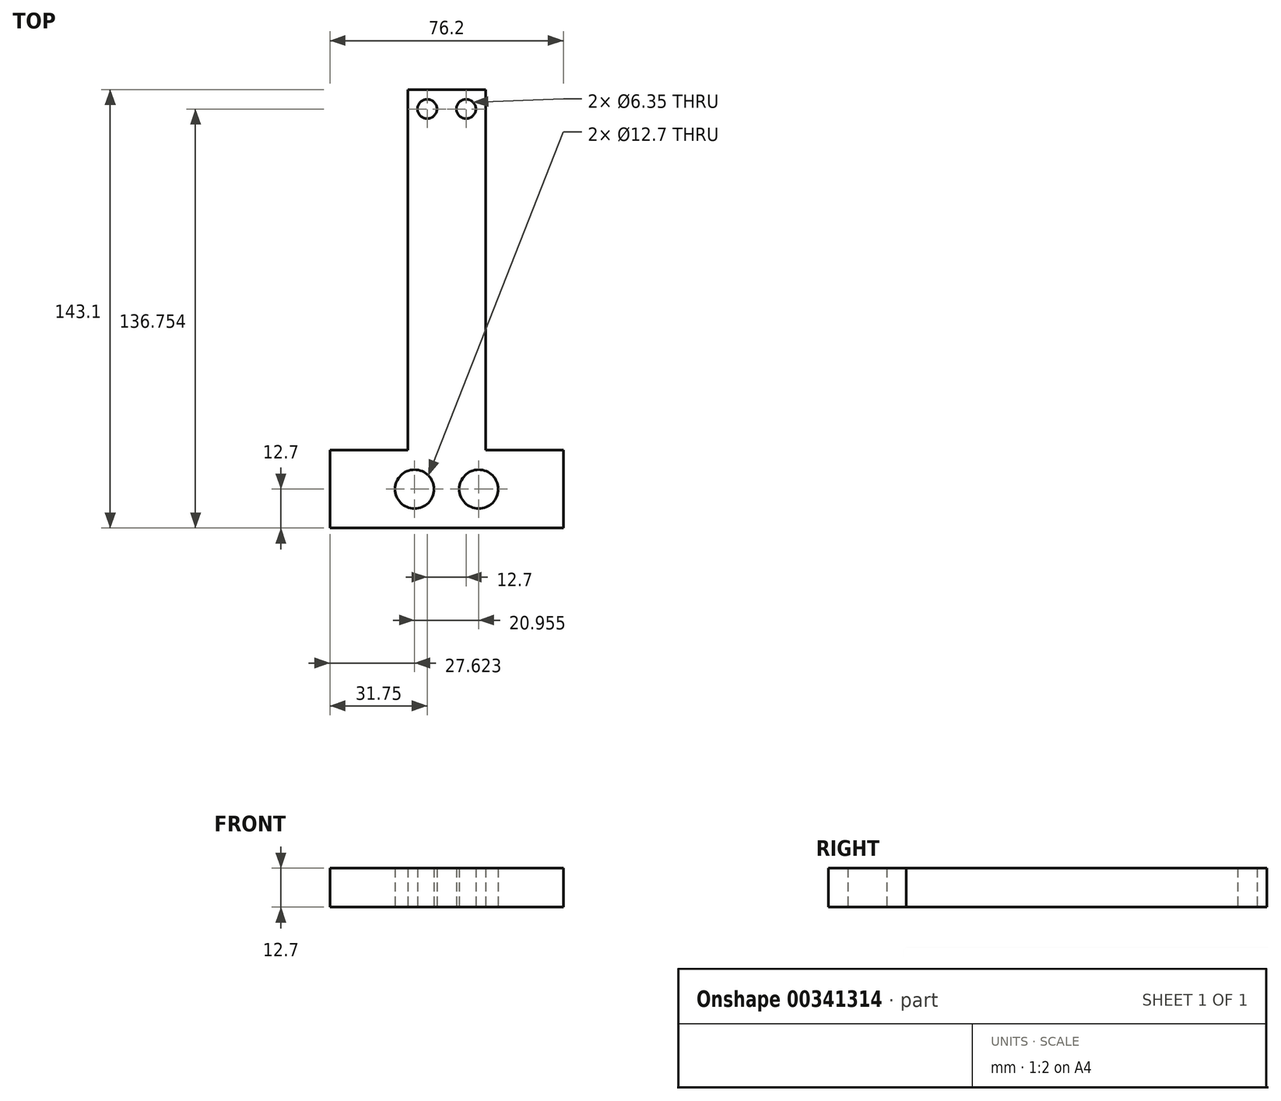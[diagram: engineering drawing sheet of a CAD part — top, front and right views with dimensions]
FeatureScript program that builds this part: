
annotation { "Feature Type Name" : "Feature", "Feature Type Description" : "" }
export const myFeature = defineFeature(function(context is Context, id is Id, definition is map)
    precondition{}
    {
        {
            var Q0;
            Q0=qCreatedBy(makeId("Top.planeOp"),FACE);
            var sketch = newSketch(context, id + "F0", { "sketchPlane" : qUnion([Q0])});
            skLineSegment(sketch, "E0.bottom", {"start": v(38.1, 12.7) * mm, "end": v(-38.1, 12.7) * mm});
            skLineSegment(sketch, "E0.top", {"start": v(38.1, -12.7) * mm, "end": v(-38.1, -12.7) * mm});
            skLineSegment(sketch, "E0.left", {"start": v(38.1, 12.7) * mm, "end": v(38.1, -12.7) * mm});
            skLineSegment(sketch, "E0.right", {"start": v(-38.1, 12.7) * mm, "end": v(-38.1, -12.7) * mm});
            skPoint(sketch, "E0.middle", {"position": v(0, 0) * mm});
            skCircle(sketch, "E1", {"center": v(-10.48, 0) * mm, "radius": 6.35 * mm});
            skCircle(sketch, "E2", {"center": v(10.48, 0) * mm, "radius": 6.35 * mm});
            skLineSegment(sketch, "E3.bottom", {"start": v(12.7, 12.7) * mm, "end": v(-12.7, 12.7) * mm});
            skLineSegment(sketch, "E3.top", {"start": v(12.7, 130.4) * mm, "end": v(-12.7, 130.4) * mm});
            skLineSegment(sketch, "E3.left", {"start": v(12.7, 12.7) * mm, "end": v(12.7, 130.4) * mm});
            skLineSegment(sketch, "E3.right", {"start": v(-12.7, 12.7) * mm, "end": v(-12.7, 130.4) * mm});
            skCircle(sketch, "E4", {"center": v(6.35, 124.05) * mm, "radius": 3.18 * mm});
            skCircle(sketch, "E5", {"center": v(-6.35, 124.05) * mm, "radius": 3.18 * mm});
            skSolve(sketch);
        }
        {
            var Q0;
            Q0 = qSketchRegion(id + "F0", true);
            extrude(context, id + "F1", {"entities" : qUnion([Q0]), "depth" : 12.7 * mm});
        }
    });
